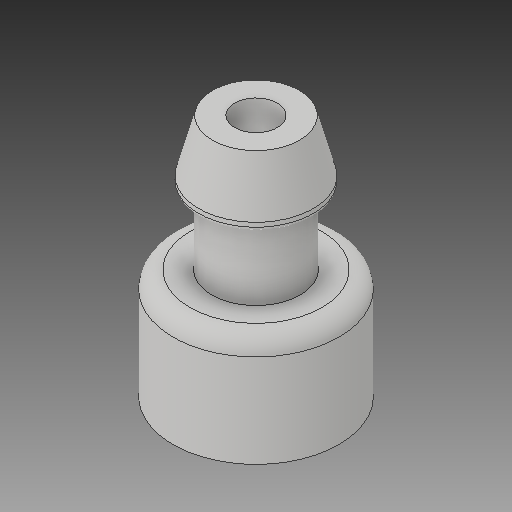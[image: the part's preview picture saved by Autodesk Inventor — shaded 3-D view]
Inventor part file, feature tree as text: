
AUTODESK INVENTOR PART (.ipt)
format: ipt  version: 2017 (Build 210142000, 142)  size: 155,648 bytes
history: native  units: in
note: dims shown in document units (in); Inventor stores cm internally (conversion verified against a paired STEP export)
features: fillet x1
ambient origin geometry x8: Origin, YZ Plane, XZ Plane, XY Plane, X Axis, Y Axis, Z Axis, Center Point
bodies: Solid1 (feature_tree)
feature tree (1):
  fillet  "Fillet1"  [1 undecoded]
note: 1 required parameter value undecoded (feature->parameter linkage not recoverable at this tier; creation-order binding heuristic only, values carry confidence <= 0.55)
